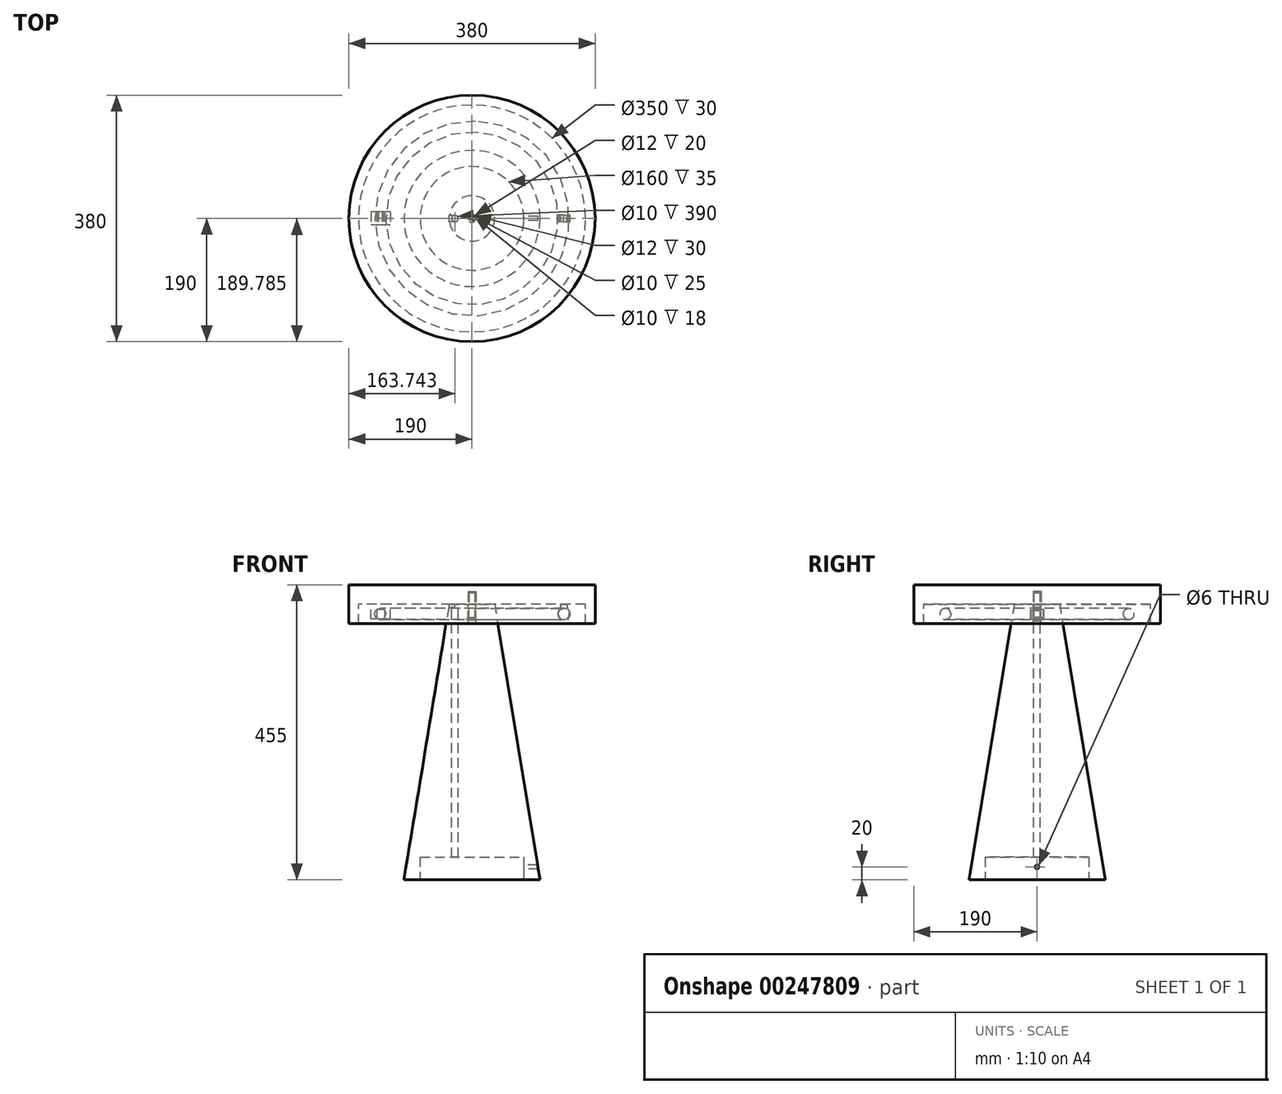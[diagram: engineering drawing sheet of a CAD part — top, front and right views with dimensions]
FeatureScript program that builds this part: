
annotation { "Feature Type Name" : "Feature", "Feature Type Description" : "" }
export const myFeature = defineFeature(function(context is Context, id is Id, definition is map)
    precondition{}
    {
        {
            var Q0;
            Q0=qCreatedBy(makeId("Front.planeOp"),FACE);
            var sketch = newSketch(context, id + "F0", { "sketchPlane" : qUnion([Q0])});
            skLineSegment(sketch, "E0", {"start": v(0, 0) * mm, "end": v(-80, 0) * mm});
            skLineSegment(sketch, "E1", {"start": v(-80, 0) * mm, "end": v(-20, 450) * mm});
            skLineSegment(sketch, "E2", {"start": v(-20, 450) * mm, "end": v(0, 450) * mm});
            skLineSegment(sketch, "E3", {"start": v(0, 450) * mm, "end": v(0, 0) * mm});
            skSolve(sketch);
        }
        {
            var Q0;
            Q0 = qSketchRegion(id + "F0", true);
            var Q1;
            Q1=sQuery(id+"F0.wireOp",EDGE,"E3");
            revolve(context, id + "F1", {"entities" : qUnion([Q0]), "axis" : qUnion([Q1]), "revolveType" : RevolveType.FULL});
        }
        {
            var Q0;
            Q0=qCreatedBy(makeId("Front.planeOp"),FACE);
            var sketch = newSketch(context, id + "F2", { "sketchPlane" : qUnion([Q0])});
            skCircle(sketch, "E4", {"center": v(-141.5, 410) * mm, "radius": 8.5 * mm});
            skLineSegment(sketch, "E5", {"start": v(-141.5, 410) * mm, "end": v(0, 410) * mm, "construction": true});
            skLineSegment(sketch, "E6", {"start": v(0, 410) * mm, "end": v(0, 0) * mm, "construction": true});
            skSolve(sketch);
        }
        {
            var Q0;
            Q0 = qSketchRegion(id + "F2", true);
            var Q1;
            Q1=sQuery(id+"F2.wireOp",EDGE,"E6");
            revolve(context, id + "F3", {"entities" : qUnion([Q0]), "axis" : qUnion([Q1]), "revolveType" : RevolveType.FULL});
        }
        {
            var Q0;
            Q0=qCreatedBy(makeId("Front.planeOp"),FACE);
            var sketch = newSketch(context, id + "F4", { "sketchPlane" : qUnion([Q0])});
            skLineSegment(sketch, "E7.bottom", {"start": v(-180, 450) * mm, "end": v(-165, 450) * mm});
            skLineSegment(sketch, "E7.top", {"start": v(-180, 500) * mm, "end": v(0, 500) * mm});
            skLineSegment(sketch, "E7.left", {"start": v(-180, 450) * mm, "end": v(-180, 500) * mm});
            skLineSegment(sketch, "E7.right", {"start": v(0, 475) * mm, "end": v(0, 500) * mm});
            skLineSegment(sketch, "E8.top", {"start": v(-20, 475) * mm, "end": v(-165, 475) * mm});
            skLineSegment(sketch, "E8.right", {"start": v(-165, 450) * mm, "end": v(-165, 475) * mm});
            skPoint(sketch, "E9.orphan", {"position": v(0, 450) * mm});
            skLineSegment(sketch, "E10.top", {"start": v(0, 450) * mm, "end": v(-20, 450) * mm});
            skLineSegment(sketch, "E10.left", {"start": v(0, 475) * mm, "end": v(0, 450) * mm});
            skLineSegment(sketch, "E10.right", {"start": v(-20, 475) * mm, "end": v(-20, 450) * mm});
            skSolve(sketch);
        }
        {
            var Q0;
            Q0 = qSketchRegion(id + "F4", true);
            var Q1;
            Q1=sQuery(id+"F4.wireOp",EDGE,"E7.right");
            revolve(context, id + "F5", {"entities" : qUnion([Q0]), "axis" : qUnion([Q1]), "revolveType" : RevolveType.FULL});
        }
        {
            var Q0;
            Q0=makeQuery(id+"F1.opRevolve","SWEPT_FACE",FACE,{"disambiguationData":[OSD([sQuery(id+"F0.wireOp",EDGE,"E0")])]});
            var sketch = newSketch(context, id + "F6", { "sketchPlane" : qUnion([Q0])});
            skCircle(sketch, "E11", {"center": v(0, 0) * mm, "radius": 6 * mm});
            skSolve(sketch);
        }
        {
            var Q0;
            Q0 = qSketchRegion(id + "F6", true);
            var Q1;
            Q1=makeQuery(id+"F5.opRevolve","SWEPT_FACE",FACE,{"disambiguationData":[OSD([sQuery(id+"F4.wireOp",EDGE,"E8.top")])]});
            extrude(context, id + "F7", {"entities" : qUnion([Q0]), "operationType" : NewBodyOperationType.REMOVE, "endBound" : BoundingType.UP_TO_SURFACE, "oppositeDirection" : true, "endBoundEntityFace" : qUnion([Q1]), "depth" : 25 * mm});
        }
        {
            var Q0;
            Q0=makeQuery(id+"F1.opRevolve","SWEPT_FACE",FACE,{"disambiguationData":[OSD([sQuery(id+"F0.wireOp",EDGE,"E0")])]});
            var sketch = newSketch(context, id + "F8", { "sketchPlane" : qUnion([Q0])});
            skLineSegment(sketch, "E12.bottom", {"start": v(33.5, -51.5) * mm, "end": v(-33.5, -51.5) * mm, "construction": true});
            skLineSegment(sketch, "E12.top", {"start": v(33.5, 51.5) * mm, "end": v(-33.5, 51.5) * mm, "construction": true});
            skLineSegment(sketch, "E12.left", {"start": v(33.5, -51.5) * mm, "end": v(33.5, 51.5) * mm, "construction": true});
            skLineSegment(sketch, "E12.right", {"start": v(-33.5, -51.5) * mm, "end": v(-33.5, 51.5) * mm, "construction": true});
            skPoint(sketch, "E12.middle", {"position": v(0, 0) * mm});
            skCircle(sketch, "E13", {"center": v(0, 0) * mm, "radius": 67.5 * mm});
            skSolve(sketch);
        }
        {
            var Q0;
            Q0=makeQuery(id+"F8.imprint","IMPRINT",FACE,{"disambiguationData":[TD([[makeQuery(id+"F8.imprint","IMPRINT",EDGE,{"derivedFrom":sQuery(id+"F8.wireOp",EDGE,"E13")}),1.0]])]});
            extrude(context, id + "F9", {"entities" : qUnion([Q0]), "operationType" : NewBodyOperationType.REMOVE, "oppositeDirection" : true, "depth" : 30 * mm});
        }
        {
            var Q0;
            Q0=qCreatedBy(makeId("Front.planeOp"),FACE);
            var sketch = newSketch(context, id + "F10", { "sketchPlane" : qUnion([Q0])});
            skLineSegment(sketch, "E14.bottom", {"start": v(-5.89, 475.17) * mm, "end": v(-4.89, 475.17) * mm});
            skLineSegment(sketch, "E14.top", {"start": v(-5.89, 450.17) * mm, "end": v(-4.89, 450.17) * mm});
            skLineSegment(sketch, "E14.left", {"start": v(-5.89, 475.17) * mm, "end": v(-5.89, 450.17) * mm});
            skLineSegment(sketch, "E14.right", {"start": v(0.11, 475.17) * mm, "end": v(0.11, 450.17) * mm, "construction": true});
            skLineSegment(sketch, "E15.right", {"start": v(-4.89, 475.17) * mm, "end": v(-4.89, 450.17) * mm});
            skSolve(sketch);
        }
        {
            var Q0;
            Q0 = qSketchRegion(id + "F10", true);
            var Q1;
            Q1=sQuery(id+"F10.wireOp",EDGE,"E14.right");
            revolve(context, id + "F11", {"entities" : qUnion([Q0]), "axis" : qUnion([Q1]), "revolveType" : RevolveType.FULL});
        }
        {
            var Q0;
            Q0=qCreatedBy(makeId("Front.planeOp"),FACE);
            var sketch = newSketch(context, id + "F12", { "sketchPlane" : qUnion([Q0])});
            skLineSegment(sketch, "E16.bottom", {"start": v(-6, 449.94) * mm, "end": v(-5, 449.94) * mm});
            skLineSegment(sketch, "E16.top", {"start": v(-6, 424.94) * mm, "end": v(-5, 424.94) * mm});
            skLineSegment(sketch, "E16.left", {"start": v(-6, 449.94) * mm, "end": v(-6, 424.94) * mm});
            skLineSegment(sketch, "E16.right", {"start": v(0, 449.94) * mm, "end": v(0, 424.94) * mm, "construction": true});
            skLineSegment(sketch, "E17.right", {"start": v(-5, 449.94) * mm, "end": v(-5, 424.94) * mm});
            skSolve(sketch);
        }
        {
            var Q0;
            Q0 = qSketchRegion(id + "F12", true);
            var Q1;
            Q1=sQuery(id+"F12.wireOp",EDGE,"E16.right");
            revolve(context, id + "F13", {"entities" : qUnion([Q0]), "axis" : qUnion([Q1]), "revolveType" : RevolveType.FULL});
        }
        {
            var Q0;
            Q0=qCreatedBy(makeId("Front.planeOp"),FACE);
            var sketch = newSketch(context, id + "F14", { "sketchPlane" : qUnion([Q0])});
            skLineSegment(sketch, "E18.bottom", {"start": v(0, 424.9) * mm, "end": v(-2.5, 424.9) * mm});
            skLineSegment(sketch, "E18.top", {"start": v(0, 474.9) * mm, "end": v(-5, 474.9) * mm});
            skLineSegment(sketch, "E18.left", {"start": v(0, 424.9) * mm, "end": v(0, 474.9) * mm});
            skLineSegment(sketch, "E18.right", {"start": v(-5, 424.9) * mm, "end": v(-5, 474.9) * mm});
            skLineSegment(sketch, "E19.left", {"start": v(0, 474.9) * mm, "end": v(0, 424.9) * mm, "construction": true});
            skLineSegment(sketch, "E19.right", {"start": v(-4, 474.9) * mm, "end": v(-4, 424.9) * mm});
            skPoint(sketch, "E19.top.end.orphan", {"position": v(-2.5, 424.9) * mm});
            skLineSegment(sketch, "E20.trimOffspring", {"start": v(-4, 424.9) * mm, "end": v(-5, 424.9) * mm});
            skSolve(sketch);
        }
        {
            var Q0;
            Q0 = qSketchRegion(id + "F14", true);
            var Q1;
            Q1=sQuery(id+"F14.wireOp",EDGE,"E18.left");
            revolve(context, id + "F15", {"entities" : qUnion([Q0]), "axis" : qUnion([Q1]), "revolveType" : RevolveType.FULL});
        }
        {
            var Q0;
            Q0=qCreatedBy(makeId("Front.planeOp"),FACE);
            var sketch = newSketch(context, id + "F16", { "sketchPlane" : qUnion([Q0])});
            skLineSegment(sketch, "E21", {"start": v(-30, 420.77) * mm, "end": v(0, 420.77) * mm});
            skLineSegment(sketch, "E22", {"start": v(0, 420.77) * mm, "end": v(0, 416.77) * mm});
            skLineSegment(sketch, "E23", {"start": v(0, 416.77) * mm, "end": v(-30, 416.77) * mm});
            skLineSegment(sketch, "E24", {"start": v(-30, 416.77) * mm, "end": v(-30, 420.77) * mm});
            skSolve(sketch);
        }
        {
            var Q0;
            Q0 = qSketchRegion(id + "F16", true);
            var Q1;
            Q1=sQuery(id+"F16.wireOp",EDGE,"E23");
            revolve(context, id + "F17", {"operationType" : NewBodyOperationType.REMOVE, "entities" : qUnion([Q0]), "axis" : qUnion([Q1]), "revolveType" : RevolveType.FULL, "oppositeDirection" : true});
        }
        {
            var Q0;
            Q0=qCreatedBy(makeId("Front.planeOp"),FACE);
            var sketch = newSketch(context, id + "F18", { "sketchPlane" : qUnion([Q0])});
            skLineSegment(sketch, "E25.bottom", {"start": v(-47.82, 0) * mm, "end": v(-102.82, 0) * mm});
            skLineSegment(sketch, "E25.right", {"start": v(-102.82, 0) * mm, "end": v(-102.82, 450) * mm});
            skLineSegment(sketch, "E26", {"start": v(-47.82, 0) * mm, "end": v(-47.82, 450.05) * mm});
            skLineSegment(sketch, "E27", {"start": v(-47.82, 450.05) * mm, "end": v(-102.82, 450) * mm});
            skSolve(sketch);
        }
        {
            var Q0;
            Q0 = qSketchRegion(id + "F18", true);
            var Q1;
            Q1=sQuery(id+"F18.wireOp",EDGE,"E26");
            revolve(context, id + "F19", {"entities" : qUnion([Q0]), "axis" : qUnion([Q1]), "revolveType" : RevolveType.FULL});
        }
        {
            var Q0;
            Q0=qCreatedBy(makeId("Front.planeOp"),FACE);
            var sketch = newSketch(context, id + "F20", { "sketchPlane" : qUnion([Q0])});
            skLineSegment(sketch, "E28.bottom", {"start": v(-174.47, 0) * mm, "end": v(74.26, 0) * mm});
            skLineSegment(sketch, "E28.top", {"start": v(-174.47, 150) * mm, "end": v(74.26, 150) * mm});
            skLineSegment(sketch, "E28.left", {"start": v(-174.47, 0) * mm, "end": v(-174.47, 150) * mm});
            skLineSegment(sketch, "E28.right", {"start": v(74.26, 0) * mm, "end": v(74.26, 150) * mm});
            skSolve(sketch);
        }
        {
            var Q0;
            Q0 = qSketchRegion(id + "F20", true);
            extrude(context, id + "F21", {"entities" : qUnion([Q0]), "operationType" : NewBodyOperationType.REMOVE, "endBound" : BoundingType.THROUGH_ALL, "oppositeDirection" : true, "depth" : 25 * mm, "hasSecondDirection" : true, "secondDirectionBound" : SecondDirectionBoundingType.THROUGH_ALL, "secondDirectionOppositeDirection" : false, "secondDirectionDepth" : 25 * mm});
        }
        {
            var Q0;
            Q0=qCreatedBy(makeId("Front.planeOp"),FACE);
            var sketch = newSketch(context, id + "F22", { "sketchPlane" : qUnion([Q0])});
            skLineSegment(sketch, "E29", {"start": v(0, 0) * mm, "end": v(0, 425) * mm});
            skLineSegment(sketch, "E30", {"start": v(0, 425) * mm, "end": v(-35, 425) * mm});
            skLineSegment(sketch, "E31", {"start": v(-35, 425) * mm, "end": v(-105, 0) * mm});
            skLineSegment(sketch, "E32", {"start": v(-105, 0) * mm, "end": v(0, 0) * mm});
            skSolve(sketch);
        }
        {
            var Q0;
            Q0 = qSketchRegion(id + "F22", true);
            var Q1;
            Q1=sQuery(id+"F22.wireOp",EDGE,"E29");
            revolve(context, id + "F23", {"entities" : qUnion([Q0]), "axis" : qUnion([Q1]), "revolveType" : RevolveType.FULL});
        }
        {
            var Q0;
            Q0=qCreatedBy(makeId("Front.planeOp"),FACE);
            var sketch = newSketch(context, id + "F24", { "sketchPlane" : qUnion([Q0])});
            skLineSegment(sketch, "E33", {"start": v(0, 425) * mm, "end": v(-175, 425) * mm});
            skLineSegment(sketch, "E34", {"start": v(-190, 395) * mm, "end": v(-190, 455) * mm});
            skLineSegment(sketch, "E35", {"start": v(-190, 455) * mm, "end": v(0, 455) * mm});
            skLineSegment(sketch, "E36", {"start": v(0, 455) * mm, "end": v(0, 425) * mm});
            skLineSegment(sketch, "E37", {"start": v(-190, 395) * mm, "end": v(-175, 395) * mm});
            skLineSegment(sketch, "E38", {"start": v(-175, 395) * mm, "end": v(-175, 425) * mm});
            skSolve(sketch);
        }
        {
            var Q0;
            Q0 = qSketchRegion(id + "F24", true);
            var Q1;
            Q1=sQuery(id+"F24.wireOp",EDGE,"E36");
            revolve(context, id + "F25", {"entities" : qUnion([Q0]), "axis" : qUnion([Q1]), "revolveType" : RevolveType.FULL});
        }
        {
            var Q0;
            Q0=makeQuery(id+"F23.opRevolve","SWEPT_FACE",FACE,{"disambiguationData":[OSD([sQuery(id+"F22.wireOp",EDGE,"E30")])]});
            var sketch = newSketch(context, id + "F26", { "sketchPlane" : qUnion([Q0])});
            skCircle(sketch, "E39", {"center": v(0, 0) * mm, "radius": 6 * mm});
            skSolve(sketch);
        }
        {
            var Q0;
            Q0 = qSketchRegion(id + "F26", true);
            extrude(context, id + "F27", {"entities" : qUnion([Q0]), "operationType" : NewBodyOperationType.REMOVE, "oppositeDirection" : true, "depth" : 30 * mm});
        }
        {
            var Q0;
            Q0=makeQuery(id+"F23.opRevolve","SWEPT_FACE",FACE,{"disambiguationData":[OSD([sQuery(id+"F22.wireOp",EDGE,"E30")])]});
            var sketch = newSketch(context, id + "F28", { "sketchPlane" : qUnion([Q0])});
            skCircle(sketch, "E40", {"center": v(-26.26, -0.22) * mm, "radius": 5 * mm});
            skSolve(sketch);
        }
        {
            var Q0;
            Q0 = qSketchRegion(id + "F28", true);
            extrude(context, id + "F29", {"entities" : qUnion([Q0]), "operationType" : NewBodyOperationType.REMOVE, "endBound" : BoundingType.THROUGH_ALL, "oppositeDirection" : true, "depth" : 25 * mm});
        }
        {
            var Q0;
            Q0=makeQuery(id+"F23.opRevolve","SWEPT_FACE",FACE,{"disambiguationData":[OSD([sQuery(id+"F22.wireOp",EDGE,"E30")])]});
            var sketch = newSketch(context, id + "F30", { "sketchPlane" : qUnion([Q0])});
            skLineSegment(sketch, "E41.bottom", {"start": v(-26.33, 4.78) * mm, "end": v(-44.13, 4.78) * mm});
            skLineSegment(sketch, "E41.top", {"start": v(-26.33, -5.21) * mm, "end": v(-44.13, -5.21) * mm});
            skLineSegment(sketch, "E41.right", {"start": v(-44.13, 4.78) * mm, "end": v(-44.13, -5.21) * mm});
            skLineSegment(sketch, "E42", {"start": v(-26.33, -5.21) * mm, "end": v(-26.33, 4.78) * mm});
            skSolve(sketch);
        }
        {
            var Q0;
            Q0 = qSketchRegion(id + "F30", true);
            extrude(context, id + "F31", {"entities" : qUnion([Q0]), "operationType" : NewBodyOperationType.REMOVE, "oppositeDirection" : true, "depth" : 5 * mm});
        }
        {
            var Q0;
            Q0=makeQuery(id+"F25.opRevolve","SWEPT_FACE",FACE,{"disambiguationData":[OSD([sQuery(id+"F24.wireOp",EDGE,"E33")])]});
            var sketch = newSketch(context, id + "F32", { "sketchPlane" : qUnion([Q0])});
            skLineSegment(sketch, "E43.bottom", {"start": v(-126, -10) * mm, "end": v(-156, -10) * mm});
            skLineSegment(sketch, "E43.top", {"start": v(-126, 10) * mm, "end": v(-156, 10) * mm});
            skLineSegment(sketch, "E43.left", {"start": v(-126, -10) * mm, "end": v(-126, 10) * mm});
            skLineSegment(sketch, "E43.right", {"start": v(-156, -10) * mm, "end": v(-156, 10) * mm});
            skPoint(sketch, "E43.middle", {"position": v(-141, 0) * mm});
            skSolve(sketch);
        }
        {
            var Q0;
            Q0 = qSketchRegion(id + "F32", true);
            extrude(context, id + "F33", {"entities" : qUnion([Q0]), "depth" : 23 * mm});
        }
        {
            var Q0;
            Q0=makeQuery(id+"F33.opExtrude","CAP_FACE",FACE,{"disambiguationData":[OSD([sQuery(id+"F32.wireOp",EDGE,"E43.bottom"),sQuery(id+"F32.wireOp",EDGE,"E43.top"),sQuery(id+"F32.wireOp",EDGE,"E43.left"),sQuery(id+"F32.wireOp",EDGE,"E43.right")])],"isStart":false});
            var sketch = newSketch(context, id + "F34", { "sketchPlane" : qUnion([Q0])});
            skLineSegment(sketch, "E44.bottom", {"start": v(-135.1, -10) * mm, "end": v(-146.9, -10) * mm});
            skLineSegment(sketch, "E44.top", {"start": v(-135.1, 10) * mm, "end": v(-146.9, 10) * mm});
            skLineSegment(sketch, "E44.left", {"start": v(-135.1, -10) * mm, "end": v(-135.1, 10) * mm});
            skLineSegment(sketch, "E44.right", {"start": v(-146.9, -10) * mm, "end": v(-146.9, 10) * mm});
            skPoint(sketch, "E44.middle", {"position": v(-141, 0) * mm});
            skPoint(sketch, "E44.middle.positionSnap0", {"position": v(-141, 10) * mm});
            skPoint(sketch, "E44.centerSnap0", {"position": v(-141, 10) * mm});
            skSolve(sketch);
        }
        {
            var Q0;
            Q0 = qSketchRegion(id + "F34", true);
            extrude(context, id + "F35", {"entities" : qUnion([Q0]), "operationType" : NewBodyOperationType.REMOVE, "oppositeDirection" : true, "depth" : 15 * mm});
        }
        {
            var Q0;
            Q0=qCreatedBy(makeId("Front.planeOp"),FACE);
            var sketch = newSketch(context, id + "F36", { "sketchPlane" : qUnion([Q0])});
            skLineSegment(sketch, "E45", {"start": v(141.56, 425) * mm, "end": v(136.56, 425) * mm});
            skLineSegment(sketch, "E46", {"start": v(136.56, 425) * mm, "end": v(136.56, 418) * mm});
            skArc(sketch, "E47", {"start": v(136.56, 418) * mm, "mid": v(132.3, 410.87) * mm, "end": v(135.2, 403.1) * mm});
            skArc(sketch, "E48", {"start": v(136.1, 399.97) * mm, "mid": v(136.11, 401.66) * mm, "end": v(135.2, 403.1) * mm});
            skLineSegment(sketch, "E49", {"start": v(141.56, 425) * mm, "end": v(141.84, 410) * mm, "construction": true});
            skPoint(sketch, "E50.MirrorCS.start.orphan", {"position": v(141.56, 425) * mm});
            skPoint(sketch, "E51.MirrorCS.start.orphan", {"position": v(146.56, 425.19) * mm});
            skPoint(sketch, "E52.MirrorCS.start.orphan", {"position": v(146.82, 418.2) * mm});
            skPoint(sketch, "E53.MirrorCS.end.orphan", {"position": v(148.74, 403.35) * mm});
            skPoint(sketch, "E53.MirrorCS.start.orphan", {"position": v(147.96, 400.2) * mm});
            skLineSegment(sketch, "E54.MirrorCS", {"start": v(141.56, 425) * mm, "end": v(146.56, 425.19) * mm});
            skLineSegment(sketch, "E55.MirrorCS", {"start": v(146.56, 425.19) * mm, "end": v(146.82, 418.2) * mm});
            skArc(sketch, "E56.MirrorCS", {"start": v(146.82, 418.2) * mm, "mid": v(151.35, 411.23) * mm, "end": v(148.74, 403.35) * mm});
            skArc(sketch, "E57.MirrorCS", {"start": v(147.96, 400.2) * mm, "mid": v(147.88, 401.88) * mm, "end": v(148.74, 403.35) * mm});
            skArc(sketch, "E58.0", {"start": v(147.67, 400.1) * mm, "mid": v(147.6, 401.95) * mm, "end": v(148.53, 403.56) * mm});
            skArc(sketch, "E58.1", {"start": v(146.53, 418.02) * mm, "mid": v(151.04, 411.28) * mm, "end": v(148.53, 403.56) * mm});
            skLineSegment(sketch, "E58.2", {"start": v(146.27, 424.88) * mm, "end": v(146.53, 418.02) * mm});
            skLineSegment(sketch, "E58.3", {"start": v(141.56, 424.7) * mm, "end": v(146.27, 424.88) * mm});
            skArc(sketch, "E58.4", {"start": v(136.4, 399.88) * mm, "mid": v(136.4, 401.74) * mm, "end": v(135.4, 403.31) * mm});
            skArc(sketch, "E58.5", {"start": v(136.86, 417.83) * mm, "mid": v(132.6, 410.93) * mm, "end": v(135.4, 403.31) * mm});
            skLineSegment(sketch, "E58.6", {"start": v(136.86, 424.7) * mm, "end": v(136.86, 417.83) * mm});
            skLineSegment(sketch, "E58.7", {"start": v(141.56, 424.7) * mm, "end": v(136.86, 424.7) * mm});
            skLineSegment(sketch, "E59", {"start": v(136.4, 399.88) * mm, "end": v(136.1, 399.97) * mm});
            skLineSegment(sketch, "E60", {"start": v(147.67, 400.1) * mm, "end": v(147.96, 400.2) * mm});
            skSolve(sketch);
        }
        {
            var Q0;
            Q0 = qSketchRegion(id + "F36", true);
            extrude(context, id + "F37", {"entities" : qUnion([Q0]), "depth" : 5 * mm, "hasSecondDirection" : true, "secondDirectionOppositeDirection" : true, "secondDirectionDepth" : 5 * mm});
        }
        {
            var Q0;
            Q0=makeQuery(id+"F23.opRevolve","SWEPT_FACE",FACE,{"disambiguationData":[OSD([sQuery(id+"F22.wireOp",EDGE,"E30")])]});
            var sketch = newSketch(context, id + "F38", { "sketchPlane" : qUnion([Q0])});
            skCircle(sketch, "E61", {"center": v(0, 0) * mm, "radius": 5 * mm});
            skCircle(sketch, "E62", {"center": v(0, 0) * mm, "radius": 6 * mm});
            skSolve(sketch);
        }
        {
            var Q0;
            Q0 = qSketchRegion(id + "F38", true);
            extrude(context, id + "F39", {"entities" : qUnion([Q0]), "oppositeDirection" : true, "depth" : 25 * mm});
        }
        {
            var Q0;
            Q0=makeQuery(id+"F23.opRevolve","SWEPT_FACE",FACE,{"disambiguationData":[OSD([sQuery(id+"F22.wireOp",EDGE,"E32")])]});
            var sketch = newSketch(context, id + "F40", { "sketchPlane" : qUnion([Q0])});
            skCircle(sketch, "E63", {"center": v(0, 0) * mm, "radius": 80 * mm});
            skSolve(sketch);
        }
        {
            var Q0;
            Q0 = qSketchRegion(id + "F40", true);
            extrude(context, id + "F41", {"entities" : qUnion([Q0]), "operationType" : NewBodyOperationType.REMOVE, "oppositeDirection" : true, "depth" : 35 * mm});
        }
        {
            var Q0;
            Q0=makeQuery(id+"F19.opRevolve","SWEPT_BODY",BODY,{"disambiguationData":[OSD([sQuery(id+"F18.wireOp",EDGE,"E25.bottom"),sQuery(id+"F18.wireOp",EDGE,"E25.right"),sQuery(id+"F18.wireOp",EDGE,"E26"),sQuery(id+"F18.wireOp",EDGE,"E27")])]});
            var Q1;
            Q1=makeQuery(id+"F5.opRevolve","SWEPT_BODY",BODY,{"disambiguationData":[OSD([sQuery(id+"F4.wireOp",EDGE,"E7.bottom"),sQuery(id+"F4.wireOp",EDGE,"E7.top"),sQuery(id+"F4.wireOp",EDGE,"E7.left"),sQuery(id+"F4.wireOp",EDGE,"E7.right"),sQuery(id+"F4.wireOp",EDGE,"E8.top"),sQuery(id+"F4.wireOp",EDGE,"E8.right"),sQuery(id+"F4.wireOp",EDGE,"E10.top"),sQuery(id+"F4.wireOp",EDGE,"E10.left"),sQuery(id+"F4.wireOp",EDGE,"E10.right")])]});
            var Q2;
            Q2=makeQuery(id+"F11.opRevolve","SWEPT_BODY",BODY,{"disambiguationData":[OSD([sQuery(id+"F10.wireOp",EDGE,"E14.bottom"),sQuery(id+"F10.wireOp",EDGE,"E14.top"),sQuery(id+"F10.wireOp",EDGE,"E14.left"),sQuery(id+"F10.wireOp",EDGE,"E15.right")])]});
            var Q3;
            Q3=makeQuery(id+"F13.opRevolve","SWEPT_BODY",BODY,{"disambiguationData":[OSD([sQuery(id+"F12.wireOp",EDGE,"E16.bottom"),sQuery(id+"F12.wireOp",EDGE,"E16.top"),sQuery(id+"F12.wireOp",EDGE,"E16.left"),sQuery(id+"F12.wireOp",EDGE,"E17.right")])]});
            var Q4;
            Q4=makeQuery(id+"F15.opRevolve","SWEPT_BODY",BODY,{"disambiguationData":[OSD([sQuery(id+"F14.wireOp",EDGE,"E18.top"),sQuery(id+"F14.wireOp",EDGE,"E18.right"),sQuery(id+"F14.wireOp",EDGE,"E19.right"),sQuery(id+"F14.wireOp",EDGE,"E20.trimOffspring")])]});
            var Q5;
            Q5=makeQuery(id+"F1.opRevolve","SWEPT_BODY",BODY,{"disambiguationData":[OSD([sQuery(id+"F0.wireOp",EDGE,"E0"),sQuery(id+"F0.wireOp",EDGE,"E1"),sQuery(id+"F0.wireOp",EDGE,"E2"),sQuery(id+"F0.wireOp",EDGE,"E3")])]});
            deleteBodies(context, id + "F42", {"entities" : qUnion([Q0, Q1, Q2, Q3, Q4, Q5])});
        }
        {
            var Q0;
            Q0=qCreatedBy(makeId("Right.planeOp"),FACE);
            var sketch = newSketch(context, id + "F43", { "sketchPlane" : qUnion([Q0])});
            skCircle(sketch, "E64", {"center": v(0, 20) * mm, "radius": 3 * mm});
            skSolve(sketch);
        }
        {
            var Q0;
            Q0 = qSketchRegion(id + "F43", true);
            extrude(context, id + "F44", {"entities" : qUnion([Q0]), "operationType" : NewBodyOperationType.REMOVE, "endBound" : BoundingType.THROUGH_ALL, "depth" : 25 * mm});
        }
        {
            var Q0;
            Q0=makeQuery(id+"F25.opRevolve","SWEPT_FACE",FACE,{"disambiguationData":[OSD([sQuery(id+"F24.wireOp",EDGE,"E33")])]});
            var sketch = newSketch(context, id + "F45", { "sketchPlane" : qUnion([Q0])});
            skCircle(sketch, "E65", {"center": v(0, 0) * mm, "radius": 6 * mm});
            skSolve(sketch);
        }
        {
            var Q0;
            Q0 = qSketchRegion(id + "F45", true);
            extrude(context, id + "F46", {"entities" : qUnion([Q0]), "operationType" : NewBodyOperationType.REMOVE, "oppositeDirection" : true, "depth" : 20 * mm});
        }
        {
            var Q0;
            Q0=makeQuery(id+"F25.opRevolve","SWEPT_FACE",FACE,{"disambiguationData":[OSD([sQuery(id+"F24.wireOp",EDGE,"E33")])]});
            var sketch = newSketch(context, id + "F47", { "sketchPlane" : qUnion([Q0])});
            skCircle(sketch, "E66", {"center": v(0, 0) * mm, "radius": 6 * mm});
            skCircle(sketch, "E67", {"center": v(0, 0) * mm, "radius": 5 * mm});
            skSolve(sketch);
        }
        {
            var Q0;
            Q0 = qSketchRegion(id + "F47", true);
            extrude(context, id + "F48", {"entities" : qUnion([Q0]), "oppositeDirection" : true, "depth" : 18 * mm});
        }
        {
            var Q0;
            Q0=makeQuery(id+"F25.opRevolve","SWEPT_FACE",FACE,{"disambiguationData":[OSD([sQuery(id+"F24.wireOp",EDGE,"E33")])]});
            var sketch = newSketch(context, id + "F49", { "sketchPlane" : qUnion([Q0])});
            skCircle(sketch, "E68", {"center": v(0, 0) * mm, "radius": 5 * mm});
            skSolve(sketch);
        }
        {
            var Q0;
            Q0 = qSketchRegion(id + "F49", true);
            extrude(context, id + "F50", {"entities" : qUnion([Q0]), "depth" : 20 * mm, "hasSecondDirection" : true, "secondDirectionOppositeDirection" : true, "secondDirectionDepth" : 20 * mm});
        }
    });
